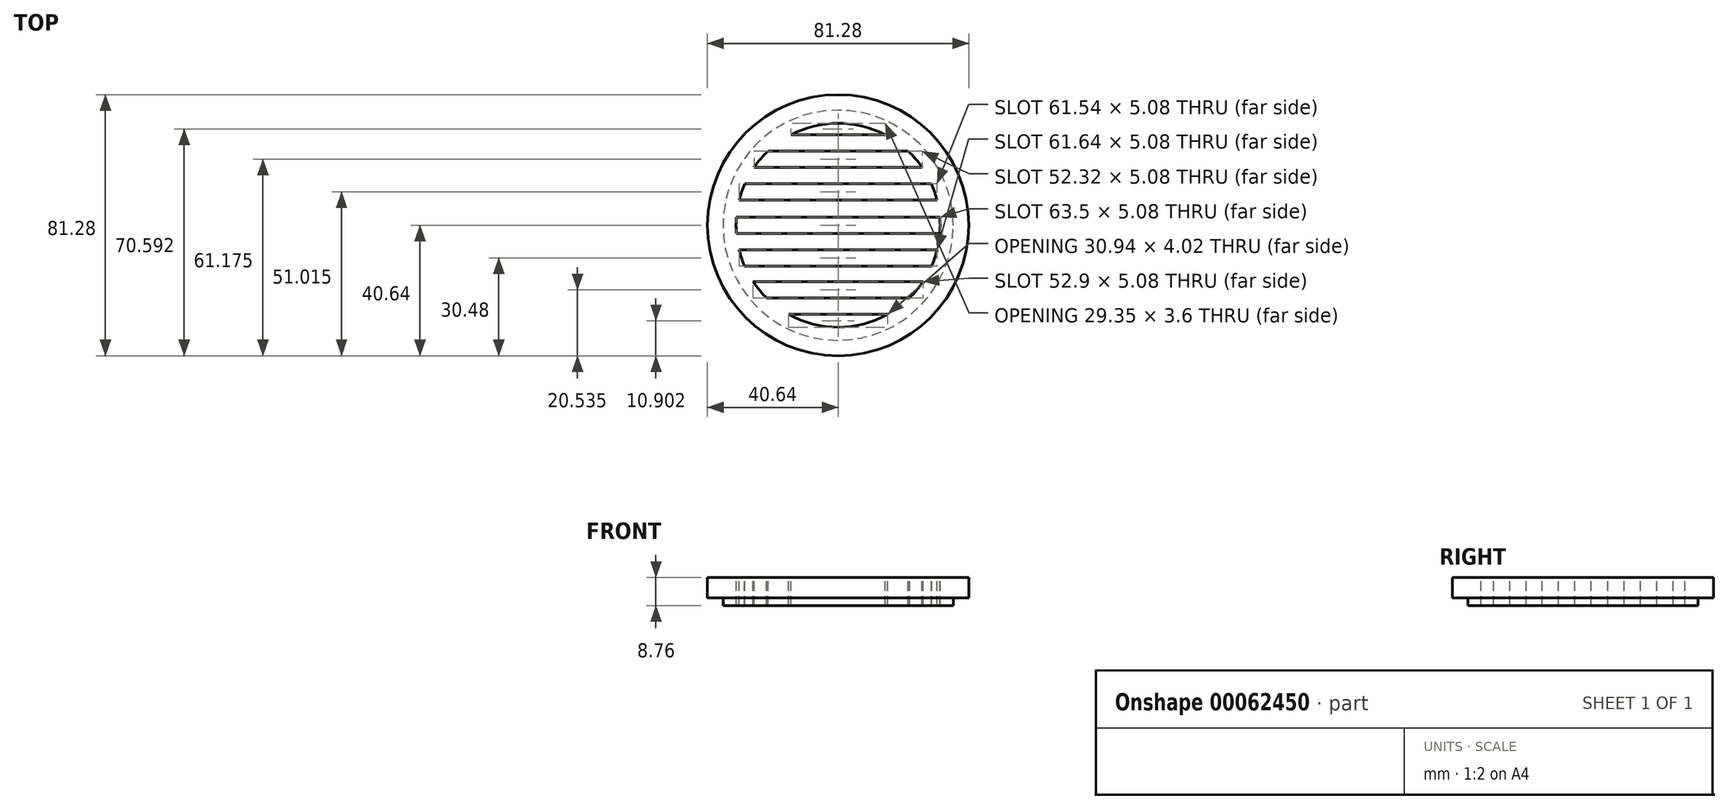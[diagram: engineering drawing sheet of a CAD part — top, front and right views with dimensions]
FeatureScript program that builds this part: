
annotation { "Feature Type Name" : "Feature", "Feature Type Description" : "" }
export const myFeature = defineFeature(function(context is Context, id is Id, definition is map)
    precondition{}
    {
        {
            var Q0;
            Q0=qCreatedBy(makeId("Top.planeOp"),FACE);
            var sketch = newSketch(context, id + "F0", { "sketchPlane" : qUnion([Q0])});
            skCircle(sketch, "E0", {"center": v(0, 0) * mm, "radius": 40.64 * mm});
            skCircle(sketch, "E1", {"center": v(0, 0) * mm, "radius": 2.54 * mm});
            skSolve(sketch);
        }
        {
            var Q0;
            Q0=qSketchRegion(id+"F0",true);
            extrude(context, id + "F1", {"entities" : qUnion([Q0]), "offsetDistance" : 25.4 * mm, "depth" : 6.35 * mm});
        }
        {
            var Q0;
            Q0=makeQuery(id+"F1.opExtrude","CAP_FACE",FACE,{"disambiguationData":[OSD([sQuery(id+"F0.wireOp",EDGE,"E0"),sQuery(id+"F0.wireOp",EDGE,"E1")])],"isStart":false});
            var sketch = newSketch(context, id + "F2", { "sketchPlane" : qUnion([Q0])});
            skArc(sketch, "E2", {"start": v(26.16, 18) * mm, "mid": v(24.12, 20.65) * mm, "end": v(21.8, 23.07) * mm});
            skLineSegment(sketch, "E3.bottom", {"start": v(-31.65, 2.54) * mm, "end": v(31.65, 2.54) * mm});
            skLineSegment(sketch, "E3.top", {"start": v(-31.65, -2.54) * mm, "end": v(31.65, -2.54) * mm});
            skLineSegment(sketch, "E4", {"start": v(0, 0) * mm, "end": v(0, 2.54) * mm});
            skPoint(sketch, "E5.left.end.orphan", {"position": v(38.1, 7.62) * mm});
            skPoint(sketch, "E5.bottom.start.orphan", {"position": v(38.1, 12.7) * mm});
            skLineSegment(sketch, "E6.bottom", {"start": v(-30.77, 7.83) * mm, "end": v(30.77, 7.83) * mm});
            skLineSegment(sketch, "E6.top", {"start": v(-29, 12.91) * mm, "end": v(29, 12.91) * mm});
            skLineSegment(sketch, "E7.bottom", {"start": v(-26.16, 18) * mm, "end": v(26.16, 18) * mm});
            skLineSegment(sketch, "E7.top", {"start": v(-21.8, 23.07) * mm, "end": v(21.8, 23.07) * mm});
            skLineSegment(sketch, "E8.bottom", {"start": v(14.68, 28.15) * mm, "end": v(-14.68, 28.15) * mm});
            skLineSegment(sketch, "E9.bottom", {"start": v(-30.82, -7.62) * mm, "end": v(30.82, -7.62) * mm});
            skLineSegment(sketch, "E9.top", {"start": v(-29.1, -12.7) * mm, "end": v(29.1, -12.7) * mm});
            skLineSegment(sketch, "E10.bottom", {"start": v(-26.45, -17.57) * mm, "end": v(26.45, -17.57) * mm});
            skLineSegment(sketch, "E10.top", {"start": v(-22.25, -22.65) * mm, "end": v(22.25, -22.65) * mm});
            skLineSegment(sketch, "E11.bottom", {"start": v(-15.47, -27.73) * mm, "end": v(15.47, -27.73) * mm});
            skPoint(sketch, "E8.right.end.orphan", {"position": v(-19.76, 33.23) * mm});
            skPoint(sketch, "E12.orphan", {"position": v(-19.76, 28.15) * mm});
            skPoint(sketch, "E3.left.start.orphan", {"position": v(-38.1, 2.54) * mm});
            skPoint(sketch, "E13.orphan", {"position": v(-38.1, -2.54) * mm});
            skPoint(sketch, "E3.right.end.orphan", {"position": v(38.1, -2.54) * mm});
            skPoint(sketch, "E14.orphan", {"position": v(38.1, 2.54) * mm});
            skArc(sketch, "E15.trimOffspring", {"start": v(30.77, 7.83) * mm, "mid": v(30, 10.41) * mm, "end": v(29, 12.91) * mm});
            skArc(sketch, "E16.trimOffspring", {"start": v(14.68, 28.15) * mm, "mid": v(0, 31.75) * mm, "end": v(-14.68, 28.15) * mm});
            skArc(sketch, "E17.trimOffspring", {"start": v(31.65, -2.54) * mm, "mid": v(31.75, 0) * mm, "end": v(31.65, 2.54) * mm});
            skArc(sketch, "E18.trimOffspring", {"start": v(29.1, -12.7) * mm, "mid": v(30.07, -10.2) * mm, "end": v(30.82, -7.62) * mm});
            skArc(sketch, "E19.trimOffspring", {"start": v(-15.47, -27.73) * mm, "mid": v(0, -31.75) * mm, "end": v(15.47, -27.73) * mm});
            skArc(sketch, "E20.trimOffspring", {"start": v(-26.45, -17.57) * mm, "mid": v(-24.48, -20.21) * mm, "end": v(-22.25, -22.65) * mm});
            skArc(sketch, "E21.trimOffspring", {"start": v(-30.82, -7.62) * mm, "mid": v(-30.07, -10.2) * mm, "end": v(-29.1, -12.7) * mm});
            skArc(sketch, "E22.trimOffspring", {"start": v(-29, 12.91) * mm, "mid": v(-30, 10.41) * mm, "end": v(-30.77, 7.83) * mm});
            skArc(sketch, "E23.trimOffspring", {"start": v(-31.65, 2.54) * mm, "mid": v(-31.75, 0) * mm, "end": v(-31.65, -2.54) * mm});
            skArc(sketch, "E24.trimOffspring", {"start": v(-21.8, 23.07) * mm, "mid": v(-24.12, 20.65) * mm, "end": v(-26.16, 18) * mm});
            skArc(sketch, "E25", {"start": v(26.45, -17.57) * mm, "mid": v(24.48, -20.21) * mm, "end": v(22.25, -22.65) * mm});
            skSolve(sketch);
        }
        {
            var Q0;
            Q0=makeQuery(id+"F1.opExtrude","CAP_FACE",FACE,{"disambiguationData":[OSD([sQuery(id+"F0.wireOp",EDGE,"E0"),sQuery(id+"F0.wireOp",EDGE,"E1")])],"isStart":true});
            var sketch = newSketch(context, id + "F3", { "sketchPlane" : qUnion([Q0])});
            skCircle(sketch, "E26", {"center": v(0, 0) * mm, "radius": 35.81 * mm});
            skSolve(sketch);
        }
        {
            var Q0;
            Q0 = qSketchRegion(id + "F3", true);
            extrude(context, id + "F4", {"entities" : qUnion([Q0]), "operationType" : NewBodyOperationType.ADD, "depth" : 2.41 * mm, "offsetDistance" : 25.4 * mm});
        }
        {
            var Q0;
            Q0 = qSketchRegion(id + "F2", true);
            extrude(context, id + "F5", {"entities" : qUnion([Q0]), "operationType" : NewBodyOperationType.REMOVE, "endBound" : BoundingType.THROUGH_ALL, "oppositeDirection" : true, "depth" : 25.4 * mm, "offsetDistance" : 25.4 * mm});
        }
    });
